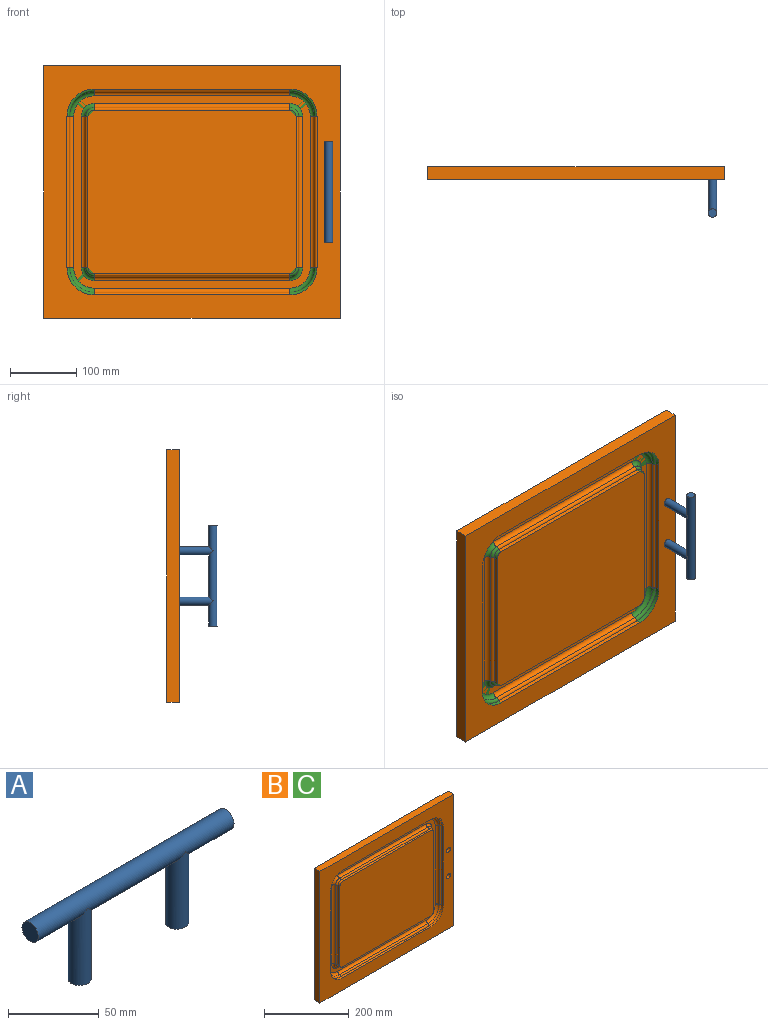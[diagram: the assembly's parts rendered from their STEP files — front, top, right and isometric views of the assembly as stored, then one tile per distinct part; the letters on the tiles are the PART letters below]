
ASSEMBLY  parts=3 mates=1
PART A: 7 faces, bbox 152.4x12.7x57.2 mm
  f0: plane 12.7x12.7mm, normal (-1,0,0), area 126.7mm2, adj f2
  f1: plane 12.7x12.7mm, normal (1,0,0), area 126.7mm2, adj f2
  f2: cylinder r=6.35mm len=152.4mm, axis (1,0,0), area 5757.9mm2, adj f0,f1,f4,f6
  f3: plane 12.7x12.7mm, normal (0,0,-1), area 126.7mm2, adj f4
  f4: cylinder r=6.35mm len=50.8mm, axis (0,0,-1), area 1865.5mm2, adj f2,f3
  f5: plane 12.7x12.7mm, normal (0,0,-1), area 126.7mm2, adj f6
  f6: cylinder r=6.35mm len=50.8mm, axis (0,0,-1), area 1865.5mm2, adj f2,f5
PART B: 58 faces, bbox 447.7x19.1x381 mm
  f0: plane 381x19.05mm, normal (-1,0,0), area 7258.1mm2, adj f1,f3,f4,f5
  f1: plane 447.68x19.05mm, normal (0,0,-1), area 8528.2mm2, adj f0,f2,f4,f5
  f2: plane 381x19.05mm, normal (1,0,0), area 7258.1mm2, adj f1,f3,f4,f5
  f3: plane 447.68x19.05mm, normal (0,0,1), area 8528.2mm2, adj f0,f2,f4,f5
  f4: plane 447.68x381mm, normal (0,-1,0), area 54213mm2, adj f0,f1,f2,f3,f11,f17,f23,f29
  f5: plane 447.68x381mm, normal (0,1,0), area 170310.8mm2, adj f0,f1,f2,f3,f56,f57
  f6: torus R=41.27mm, axis (0,1,0), area 379.4mm2, adj f7,f11,f12,f48
  f7: torus R=30.96mm, axis (0,1,0), area 548.4mm2, adj f6,f13,f49,f50
  f8: torus R=19.84mm, axis (0,1,0), area 247.6mm2, adj f9,f14,f50,f51
  f9: torus R=9.53mm, axis (0,1,0), area 118mm2, adj f8,f10,f15,f52
  f10: cylinder r=9.53mm len=9.53mm, axis (0,1,0), area 95mm2, adj f9,f16,f53,f55
  f11: cylinder r=41.27mm len=41.28mm, axis (0,1,0), area 411.7mm2, adj f4,f6,f17,f54
  f12: cylinder r=3.97mm len=295.28mm, axis (-1,0,0), area 1840.8mm2, adj f6,f13,f17,f18
  f13: cylinder r=6.35mm len=295.28mm, axis (-1,0,0), area 2945.2mm2, adj f7,f12,f19,f50
  f14: cylinder r=6.35mm len=295.28mm, axis (-1,0,0), area 2945.2mm2, adj f8,f15,f20,f50
  f15: cylinder r=3.97mm len=295.28mm, axis (-1,0,0), area 1840.8mm2, adj f9,f14,f16,f21
  f16: plane 295.28x6.35mm, normal (0,0,-1), area 1875mm2, adj f10,f15,f22,f55
  f17: plane 295.28x6.35mm, normal (0,0,1), area 1875mm2, adj f4,f11,f12,f23
  f18: torus R=41.27mm, axis (0,1,0), area 379.4mm2, adj f12,f19,f23,f24
  f19: torus R=30.96mm, axis (0,1,0), area 548.4mm2, adj f13,f18,f25,f50
  f20: torus R=19.84mm, axis (0,1,0), area 247.6mm2, adj f14,f21,f26,f50
  f21: torus R=9.53mm, axis (0,1,0), area 118mm2, adj f15,f20,f22,f27
  f22: cylinder r=9.53mm len=9.53mm, axis (0,1,0), area 95mm2, adj f16,f21,f28,f55
  f23: cylinder r=41.27mm len=41.28mm, axis (0,1,0), area 411.7mm2, adj f4,f17,f18,f29
  f24: cylinder r=3.97mm len=228.6mm, axis (0,0,-1), area 1425.1mm2, adj f18,f25,f29,f30
  f25: cylinder r=6.35mm len=228.6mm, axis (0,0,-1), area 2280.2mm2, adj f19,f24,f31,f50
  f26: cylinder r=6.35mm len=228.6mm, axis (0,0,-1), area 2280.2mm2, adj f20,f27,f32,f50
  f27: cylinder r=3.97mm len=228.6mm, axis (0,0,-1), area 1425.1mm2, adj f21,f26,f28,f33
  f28: plane 228.6x6.35mm, normal (1,0,0), area 1451.6mm2, adj f22,f27,f34,f55
  f29: plane 228.6x6.35mm, normal (-1,0,0), area 1451.6mm2, adj f4,f23,f24,f35
  f30: torus R=41.27mm, axis (0,1,0), area 379.4mm2, adj f24,f31,f35,f36
  f31: torus R=30.96mm, axis (0,1,0), area 548.4mm2, adj f25,f30,f37,f50
  f32: torus R=19.84mm, axis (0,1,0), area 247.6mm2, adj f26,f33,f38,f50
  f33: torus R=9.53mm, axis (0,1,0), area 118mm2, adj f27,f32,f34,f39
  f34: cylinder r=9.53mm len=9.53mm, axis (0,1,0), area 95mm2, adj f28,f33,f40,f55
  f35: cylinder r=41.27mm len=41.28mm, axis (0,1,0), area 411.7mm2, adj f4,f29,f30,f41
  f36: cylinder r=3.97mm len=295.28mm, axis (1,0,0), area 1840.8mm2, adj f30,f37,f41,f42
  f37: cylinder r=6.35mm len=295.28mm, axis (1,0,0), area 2945.2mm2, adj f31,f36,f43,f50
  f38: cylinder r=6.35mm len=295.28mm, axis (1,0,0), area 2945.2mm2, adj f32,f39,f44,f50
  f39: cylinder r=3.97mm len=295.28mm, axis (1,0,0), area 1840.8mm2, adj f33,f38,f40,f45
  f40: plane 295.28x6.35mm, normal (0,0,1), area 1875mm2, adj f34,f39,f46,f55
  f41: plane 295.28x6.35mm, normal (0,0,-1), area 1875mm2, adj f4,f35,f36,f47
  f42: torus R=41.27mm, axis (0,1,0), area 379.4mm2, adj f36,f43,f47,f48
  f43: torus R=30.96mm, axis (0,1,0), area 548.4mm2, adj f37,f42,f49,f50
  f44: torus R=19.84mm, axis (0,1,0), area 247.6mm2, adj f38,f45,f50,f51
  f45: torus R=9.53mm, axis (0,1,0), area 118mm2, adj f39,f44,f46,f52
  f46: cylinder r=9.53mm len=9.53mm, axis (0,1,0), area 95mm2, adj f40,f45,f53,f55
  f47: cylinder r=41.27mm len=41.28mm, axis (0,1,0), area 411.7mm2, adj f4,f41,f42,f54
  f48: cylinder r=3.97mm len=228.6mm, axis (0,0,1), area 1425.1mm2, adj f6,f42,f49,f54
  f49: cylinder r=6.35mm len=228.6mm, axis (0,0,1), area 2280.2mm2, adj f7,f43,f48,f50
  f50: plane 357.19x290.51mm, normal (0,-1,0), area 13416.6mm2, adj f7,f8,f13,f14,f19,f20,f25,f26
  f51: cylinder r=6.35mm len=228.6mm, axis (0,0,1), area 2280.2mm2, adj f8,f44,f50,f52
  f52: cylinder r=3.97mm len=228.6mm, axis (0,0,1), area 1425.1mm2, adj f9,f45,f51,f53
  f53: plane 228.6x6.35mm, normal (-1,0,0), area 1451.6mm2, adj f10,f46,f52,f55
  f54: plane 228.6x6.35mm, normal (1,0,0), area 1451.6mm2, adj f4,f11,f47,f48
  f55: plane 314.33x247.65mm, normal (0,-1,0), area 77764.7mm2, adj f10,f16,f22,f28,f34,f40,f46,f53
  f56: cylinder r=6.35mm len=19.05mm, axis (0,-1,0), area 760.1mm2, adj f4,f5
  f57: cylinder r=6.35mm len=19.05mm, axis (0,-1,0), area 760.1mm2, adj f4,f5
PART C: same geometry as B
PLACE A rot(axis=(0.58,0.58,-0.58),120deg) t=(390.44,7.29,18.62)mm
PLACE B t=(-39.78,77.14,-57.98)mm
PLACE C t=(-39.78,77.14,-57.98)mm fixed
MATE fastened C.f57 <-> A.f4  axis (0,-1,0) through (390.44,58.09,-19.88)mm
